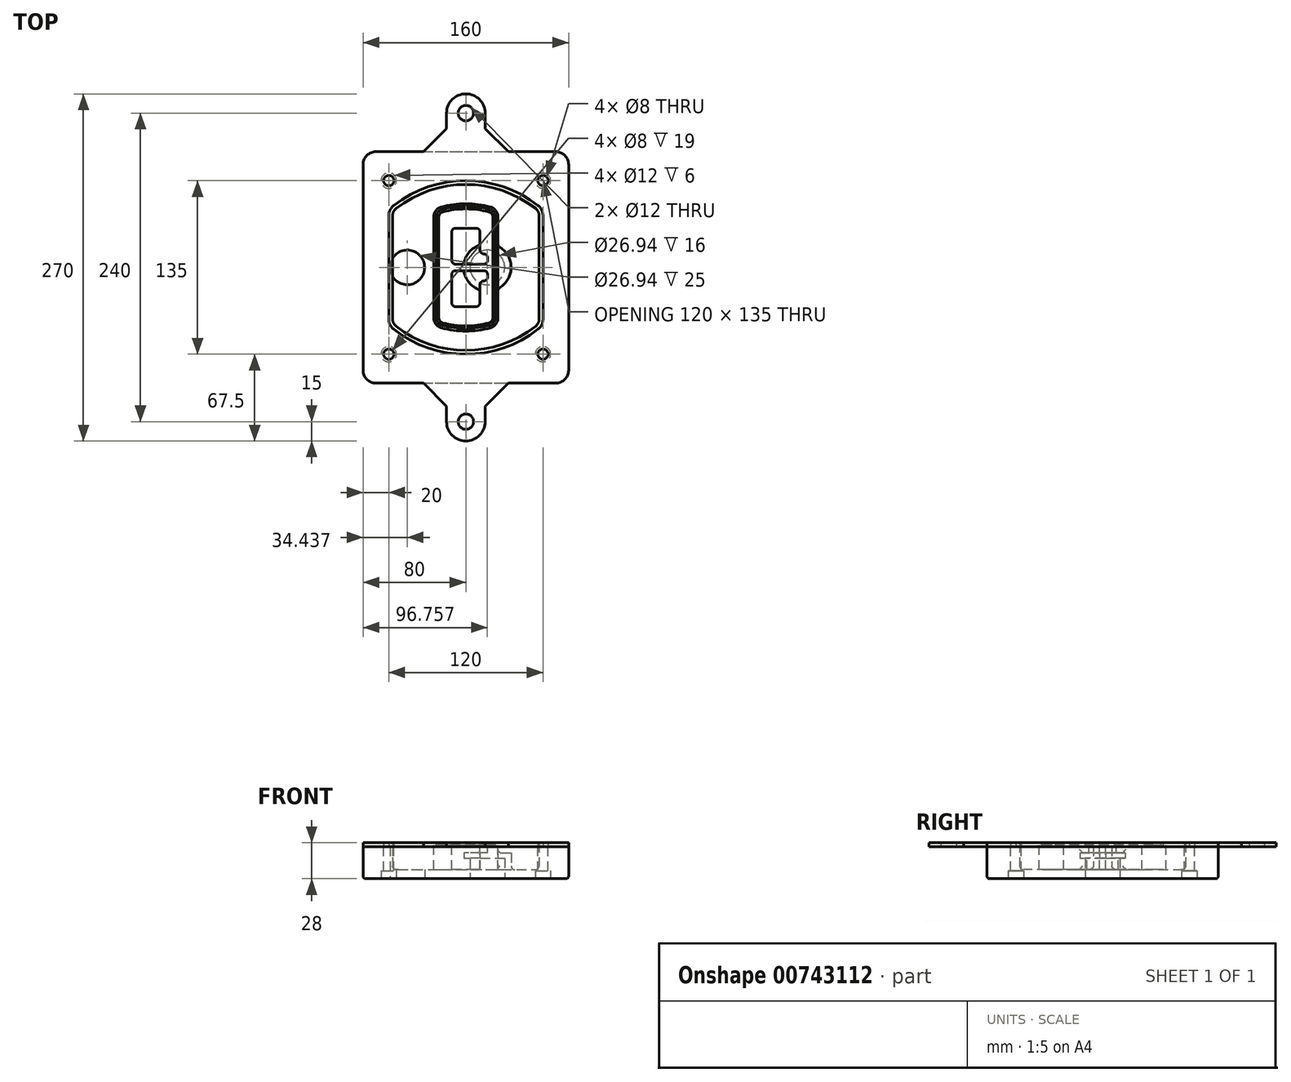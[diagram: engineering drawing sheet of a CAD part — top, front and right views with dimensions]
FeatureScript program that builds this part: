
annotation { "Feature Type Name" : "Feature", "Feature Type Description" : "" }
export const myFeature = defineFeature(function(context is Context, id is Id, definition is map)
    precondition{}
    {
        {
            var Q0;
            Q0=qCreatedBy(makeId("Top.planeOp"),FACE);
            var sketch = newSketch(context, id + "F0", { "sketchPlane" : qUnion([Q0])});
            skPoint(sketch, "E0.rect.middle", {"position": v(0, 0) * mm});
            skLineSegment(sketch, "E1.bottom", {"start": v(-70, -90) * mm, "end": v(70, -90) * mm});
            skLineSegment(sketch, "E1.top", {"start": v(-70, 90) * mm, "end": v(70, 90) * mm});
            skLineSegment(sketch, "E1.left", {"start": v(-80, -80) * mm, "end": v(-80, 80) * mm});
            skLineSegment(sketch, "E1.right", {"start": v(80, -80) * mm, "end": v(80, 80) * mm});
            skLineSegment(sketch, "E2", {"start": v(-80, 90) * mm, "end": v(80, -90) * mm, "construction": true});
            skLineSegment(sketch, "E3", {"start": v(80, 90) * mm, "end": v(-80, -90) * mm, "construction": true});
            skCircle(sketch, "E4", {"center": v(-60, 67.5) * mm, "radius": 4 * mm});
            skCircle(sketch, "E5", {"center": v(60, 67.5) * mm, "radius": 4 * mm});
            skCircle(sketch, "E6", {"center": v(60, -67.5) * mm, "radius": 4 * mm});
            skCircle(sketch, "E7", {"center": v(-60, -67.5) * mm, "radius": 4 * mm});
            skLineSegment(sketch, "E8", {"start": v(-60, 67.5) * mm, "end": v(60, 67.5) * mm, "construction": true});
            skLineSegment(sketch, "E9", {"start": v(60, 67.5) * mm, "end": v(60, -67.5) * mm, "construction": true});
            skLineSegment(sketch, "E10", {"start": v(60, -67.5) * mm, "end": v(-60, -67.5) * mm, "construction": true});
            skLineSegment(sketch, "E11", {"start": v(-60, -67.5) * mm, "end": v(-60, 67.5) * mm, "construction": true});
            skLineSegment(sketch, "E12", {"start": v(-60, 40.3) * mm, "end": v(-60, -40.3) * mm});
            skLineSegment(sketch, "E13", {"start": v(60, 40.3) * mm, "end": v(60, -40.3) * mm});
            skArc(sketch, "E14", {"start": v(56.15, 48.18) * mm, "mid": v(0, 67.5) * mm, "end": v(-56.15, 48.18) * mm});
            skArc(sketch, "E15", {"start": v(-56.15, -48.18) * mm, "mid": v(0, -67.5) * mm, "end": v(56.15, -48.18) * mm});
            skLineSegment(sketch, "E16", {"start": v(-60, 0) * mm, "end": v(60, 0) * mm, "construction": true});
            skPoint(sketch, "E17.visualSharp", {"position": v(-60, -45) * mm});
            skArc(sketch, "E17.filletArc", {"start": v(-60, -40.3) * mm, "mid": v(-58.99, -44.68) * mm, "end": v(-56.15, -48.18) * mm});
            skPoint(sketch, "E18.visualSharp", {"position": v(-60, 45) * mm});
            skArc(sketch, "E18.filletArc", {"start": v(-56.15, 48.18) * mm, "mid": v(-58.99, 44.68) * mm, "end": v(-60, 40.3) * mm});
            skPoint(sketch, "E19.visualSharp", {"position": v(60, 45) * mm});
            skArc(sketch, "E19.filletArc", {"start": v(60, 40.3) * mm, "mid": v(58.99, 44.68) * mm, "end": v(56.15, 48.18) * mm});
            skPoint(sketch, "E20.visualSharp", {"position": v(60, -45) * mm});
            skArc(sketch, "E20.filletArc", {"start": v(56.15, -48.18) * mm, "mid": v(58.99, -44.68) * mm, "end": v(60, -40.3) * mm});
            skPoint(sketch, "E21.visualSharp", {"position": v(-80, 90) * mm});
            skArc(sketch, "E21.filletArc", {"start": v(-70, 90) * mm, "mid": v(-77.07, 87.07) * mm, "end": v(-80, 80) * mm});
            skPoint(sketch, "E22.visualSharp", {"position": v(80, 90) * mm});
            skArc(sketch, "E22.filletArc", {"start": v(80, 80) * mm, "mid": v(77.07, 87.07) * mm, "end": v(70, 90) * mm});
            skPoint(sketch, "E23.visualSharp", {"position": v(80, -90) * mm});
            skArc(sketch, "E23.filletArc", {"start": v(70, -90) * mm, "mid": v(77.07, -87.07) * mm, "end": v(80, -80) * mm});
            skPoint(sketch, "E24.visualSharp", {"position": v(-80, -90) * mm});
            skArc(sketch, "E24.filletArc", {"start": v(-80, -80) * mm, "mid": v(-77.07, -87.07) * mm, "end": v(-70, -90) * mm});
            skArc(sketch, "E25.0", {"start": v(57, 40.3) * mm, "mid": v(56.3, 43.36) * mm, "end": v(54.3, 45.81) * mm});
            skLineSegment(sketch, "E25.1", {"start": v(57, 40.3) * mm, "end": v(57, -40.3) * mm});
            skArc(sketch, "E25.2", {"start": v(54.3, -45.81) * mm, "mid": v(56.3, -43.36) * mm, "end": v(57, -40.3) * mm});
            skArc(sketch, "E25.3", {"start": v(-54.3, -45.81) * mm, "mid": v(0, -64.5) * mm, "end": v(54.3, -45.81) * mm});
            skArc(sketch, "E25.4", {"start": v(-57, -40.3) * mm, "mid": v(-56.3, -43.36) * mm, "end": v(-54.3, -45.81) * mm});
            skArc(sketch, "E25.5", {"start": v(54.3, 45.81) * mm, "mid": v(0, 64.5) * mm, "end": v(-54.3, 45.81) * mm});
            skLineSegment(sketch, "E25.6", {"start": v(-57, 40.3) * mm, "end": v(-57, -40.3) * mm});
            skArc(sketch, "E25.7", {"start": v(-54.3, 45.81) * mm, "mid": v(-56.3, 43.36) * mm, "end": v(-57, 40.3) * mm});
            skArc(sketch, "E26.0", {"start": v(-58.62, 51.33) * mm, "mid": v(-62.58, 46.43) * mm, "end": v(-64, 40.3) * mm});
            skArc(sketch, "E26.1", {"start": v(58.62, 51.33) * mm, "mid": v(0, 71.5) * mm, "end": v(-58.62, 51.33) * mm});
            skArc(sketch, "E26.2", {"start": v(64, 40.3) * mm, "mid": v(62.58, 46.43) * mm, "end": v(58.62, 51.33) * mm});
            skLineSegment(sketch, "E26.3", {"start": v(64, 40.3) * mm, "end": v(64, -40.3) * mm});
            skArc(sketch, "E26.4", {"start": v(58.62, -51.33) * mm, "mid": v(62.58, -46.43) * mm, "end": v(64, -40.3) * mm});
            skLineSegment(sketch, "E26.5", {"start": v(-64, 40.3) * mm, "end": v(-64, -40.3) * mm});
            skArc(sketch, "E26.6", {"start": v(-58.62, -51.33) * mm, "mid": v(0, -71.5) * mm, "end": v(58.62, -51.33) * mm});
            skArc(sketch, "E26.7", {"start": v(-64, -40.3) * mm, "mid": v(-62.58, -46.43) * mm, "end": v(-58.62, -51.33) * mm});
            skSolve(sketch);
        }
        {
            var Q0;
            Q0=makeQuery(id+"F0.imprint","IMPRINT",FACE,{"disambiguationData":[TD([[makeQuery(id+"F0.imprint","IMPRINT",EDGE,{"derivedFrom":sQuery(id+"F0.wireOp",EDGE,"E1.bottom")}),1.0]])]});
            var Q1;
            Q1=makeQuery(id+"F0.imprint","IMPRINT",FACE,{"disambiguationData":[TD([[makeQuery(id+"F0.imprint","IMPRINT",EDGE,{"derivedFrom":sQuery(id+"F0.wireOp",EDGE,"E12")}),1.0]])]});
            var Q2;
            Q2=makeQuery(id+"F0.imprint","IMPRINT",FACE,{"disambiguationData":[TD([[makeQuery(id+"F0.imprint","IMPRINT",EDGE,{"derivedFrom":sQuery(id+"F0.wireOp",EDGE,"E25.0")}),1.0]])]});
            var Q3;
            Q3=makeQuery(id+"F0.imprint","IMPRINT",FACE,{"disambiguationData":[TD([[makeQuery(id+"F0.imprint","IMPRINT",EDGE,{"derivedFrom":sQuery(id+"F0.wireOp",EDGE,"E12")}),-1.0]])]});
            extrude(context, id + "F1", {"entities" : qUnion([Q0, Q1, Q2, Q3]), "oppositeDirection" : true, "depth" : 25 * mm});
        }
        {
            var Q0;
            Q0=makeQuery(id+"F0.imprint","IMPRINT",FACE,{"disambiguationData":[TD([[makeQuery(id+"F0.imprint","IMPRINT",EDGE,{"derivedFrom":sQuery(id+"F0.wireOp",EDGE,"E12")}),1.0]])]});
            extrude(context, id + "F2", {"entities" : qUnion([Q0]), "operationType" : NewBodyOperationType.ADD, "depth" : 3 * mm});
        }
        {
            var Q0;
            Q0=makeQuery(id+"F0.imprint","IMPRINT",FACE,{"disambiguationData":[TD([[makeQuery(id+"F0.imprint","IMPRINT",EDGE,{"derivedFrom":sQuery(id+"F0.wireOp",EDGE,"E25.0")}),1.0]])]});
            extrude(context, id + "F3", {"entities" : qUnion([Q0]), "operationType" : NewBodyOperationType.REMOVE, "oppositeDirection" : true, "depth" : 18 * mm});
        }
        {
            var Q0;
            Q0=makeQuery(id+"F2.opExtrude","CAP_FACE",FACE,{"disambiguationData":[OSD([sQuery(id+"F0.wireOp",EDGE,"E12"),sQuery(id+"F0.wireOp",EDGE,"E13"),sQuery(id+"F0.wireOp",EDGE,"E14"),sQuery(id+"F0.wireOp",EDGE,"E15"),sQuery(id+"F0.wireOp",EDGE,"E17.filletArc"),sQuery(id+"F0.wireOp",EDGE,"E18.filletArc"),sQuery(id+"F0.wireOp",EDGE,"E19.filletArc"),sQuery(id+"F0.wireOp",EDGE,"E20.filletArc"),sQuery(id+"F0.wireOp",EDGE,"E25.0"),sQuery(id+"F0.wireOp",EDGE,"E25.1"),sQuery(id+"F0.wireOp",EDGE,"E25.2"),sQuery(id+"F0.wireOp",EDGE,"E25.3"),sQuery(id+"F0.wireOp",EDGE,"E25.4"),sQuery(id+"F0.wireOp",EDGE,"E25.5"),sQuery(id+"F0.wireOp",EDGE,"E25.6"),sQuery(id+"F0.wireOp",EDGE,"E25.7")])],"isStart":false});
            var sketch = newSketch(context, id + "F4", { "sketchPlane" : qUnion([Q0])});
            skArc(sketch, "E27.0", {"start": v(-19.08, -46.97) * mm, "mid": v(0, -49.5) * mm, "end": v(19.08, -46.97) * mm});
            skArc(sketch, "E28.0", {"start": v(19.08, 46.97) * mm, "mid": v(0, 49.5) * mm, "end": v(-19.08, 46.97) * mm});
            skLineSegment(sketch, "E29", {"start": v(-25, 39.25) * mm, "end": v(-25, -39.25) * mm});
            skLineSegment(sketch, "E30", {"start": v(25, 39.25) * mm, "end": v(25, -39.25) * mm});
            skLineSegment(sketch, "E31", {"start": v(-25, 45.1) * mm, "end": v(25, 45.1) * mm, "construction": true});
            skLineSegment(sketch, "E32", {"start": v(-25, -45.1) * mm, "end": v(25, -45.1) * mm, "construction": true});
            skPoint(sketch, "E33.visualSharp", {"position": v(-25, 45.1) * mm});
            skArc(sketch, "E33.filletArc", {"start": v(-19.08, 46.97) * mm, "mid": v(-23.35, 44.11) * mm, "end": v(-25, 39.25) * mm});
            skPoint(sketch, "E34.visualSharp", {"position": v(25, 45.1) * mm});
            skArc(sketch, "E34.filletArc", {"start": v(25, 39.25) * mm, "mid": v(23.35, 44.11) * mm, "end": v(19.08, 46.97) * mm});
            skPoint(sketch, "E35.visualSharp", {"position": v(25, -45.1) * mm});
            skArc(sketch, "E35.filletArc", {"start": v(19.08, -46.97) * mm, "mid": v(23.35, -44.11) * mm, "end": v(25, -39.25) * mm});
            skPoint(sketch, "E36.visualSharp", {"position": v(-25, -45.1) * mm});
            skArc(sketch, "E36.filletArc", {"start": v(-25, -39.25) * mm, "mid": v(-23.35, -44.11) * mm, "end": v(-19.08, -46.97) * mm});
            skArc(sketch, "E37.0", {"start": v(54.3, 45.81) * mm, "mid": v(0, 64.5) * mm, "end": v(-54.3, 45.81) * mm});
            skArc(sketch, "E37.1", {"start": v(-54.3, 45.81) * mm, "mid": v(-56.3, 43.36) * mm, "end": v(-57, 40.3) * mm});
            skLineSegment(sketch, "E37.2", {"start": v(-57, 40.3) * mm, "end": v(-57, -40.3) * mm});
            skArc(sketch, "E37.3", {"start": v(-57, -40.3) * mm, "mid": v(-56.3, -43.36) * mm, "end": v(-54.3, -45.81) * mm});
            skArc(sketch, "E37.4", {"start": v(-54.3, -45.81) * mm, "mid": v(0, -64.5) * mm, "end": v(54.3, -45.81) * mm});
            skArc(sketch, "E37.5", {"start": v(54.3, -45.81) * mm, "mid": v(56.3, -43.36) * mm, "end": v(57, -40.3) * mm});
            skLineSegment(sketch, "E37.6", {"start": v(57, 40.3) * mm, "end": v(57, -40.3) * mm});
            skArc(sketch, "E37.7", {"start": v(57, 40.3) * mm, "mid": v(56.3, 43.36) * mm, "end": v(54.3, 45.81) * mm});
            skLineSegment(sketch, "E38.0", {"start": v(23, 39.25) * mm, "end": v(23, -39.25) * mm});
            skArc(sketch, "E38.1", {"start": v(18.56, -45.04) * mm, "mid": v(21.76, -42.9) * mm, "end": v(23, -39.25) * mm});
            skArc(sketch, "E38.2", {"start": v(-18.56, -45.04) * mm, "mid": v(0, -47.5) * mm, "end": v(18.56, -45.04) * mm});
            skArc(sketch, "E38.3", {"start": v(-23, -39.25) * mm, "mid": v(-21.76, -42.9) * mm, "end": v(-18.56, -45.04) * mm});
            skLineSegment(sketch, "E38.4", {"start": v(-23, 39.25) * mm, "end": v(-23, -39.25) * mm});
            skArc(sketch, "E38.5", {"start": v(23, 39.25) * mm, "mid": v(21.76, 42.9) * mm, "end": v(18.56, 45.04) * mm});
            skArc(sketch, "E38.6", {"start": v(-18.56, 45.04) * mm, "mid": v(-21.76, 42.9) * mm, "end": v(-23, 39.25) * mm});
            skArc(sketch, "E38.7", {"start": v(18.56, 45.04) * mm, "mid": v(0, 47.5) * mm, "end": v(-18.56, 45.04) * mm});
            skArc(sketch, "E39.0", {"start": v(21, 39.25) * mm, "mid": v(20.18, 41.68) * mm, "end": v(18.04, 43.1) * mm});
            skLineSegment(sketch, "E39.1", {"start": v(21, 39.25) * mm, "end": v(21, -39.25) * mm});
            skArc(sketch, "E39.2", {"start": v(18.04, -43.1) * mm, "mid": v(20.18, -41.68) * mm, "end": v(21, -39.25) * mm});
            skArc(sketch, "E39.3", {"start": v(-18.04, -43.1) * mm, "mid": v(0, -45.5) * mm, "end": v(18.04, -43.1) * mm});
            skArc(sketch, "E39.4", {"start": v(-21, -39.25) * mm, "mid": v(-20.18, -41.68) * mm, "end": v(-18.04, -43.1) * mm});
            skArc(sketch, "E39.5", {"start": v(18.04, 43.1) * mm, "mid": v(0, 45.5) * mm, "end": v(-18.04, 43.1) * mm});
            skLineSegment(sketch, "E39.6", {"start": v(-21, 39.25) * mm, "end": v(-21, -39.25) * mm});
            skArc(sketch, "E39.7", {"start": v(-18.04, 43.1) * mm, "mid": v(-20.18, 41.68) * mm, "end": v(-21, 39.25) * mm});
            skLineSegment(sketch, "E40", {"start": v(-25, 0) * mm, "end": v(25, 0) * mm, "construction": true});
            skLineSegment(sketch, "E41", {"start": v(-11, 5.5) * mm, "end": v(-11, 27.5) * mm});
            skLineSegment(sketch, "E42", {"start": v(-8, 30.5) * mm, "end": v(8, 30.5) * mm});
            skLineSegment(sketch, "E43", {"start": v(11, 27.5) * mm, "end": v(11, 13.5) * mm});
            skLineSegment(sketch, "E44", {"start": v(14, 10.5) * mm, "end": v(14, 10.5) * mm});
            skLineSegment(sketch, "E45", {"start": v(17, 7.5) * mm, "end": v(17, 5.5) * mm});
            skLineSegment(sketch, "E46", {"start": v(14, 2.5) * mm, "end": v(-8, 2.5) * mm});
            skPoint(sketch, "E47.visualSharp", {"position": v(-11, 30.5) * mm});
            skArc(sketch, "E47.filletArc", {"start": v(-8, 30.5) * mm, "mid": v(-10.12, 29.62) * mm, "end": v(-11, 27.5) * mm});
            skPoint(sketch, "E48.visualSharp", {"position": v(11, 30.5) * mm});
            skArc(sketch, "E48.filletArc", {"start": v(11, 27.5) * mm, "mid": v(10.12, 29.62) * mm, "end": v(8, 30.5) * mm});
            skPoint(sketch, "E49.visualSharp", {"position": v(11, 10.5) * mm});
            skArc(sketch, "E49.filletArc", {"start": v(11, 13.5) * mm, "mid": v(11.88, 11.38) * mm, "end": v(14, 10.5) * mm});
            skPoint(sketch, "E50.visualSharp", {"position": v(17, 10.5) * mm});
            skArc(sketch, "E50.filletArc", {"start": v(17, 7.5) * mm, "mid": v(16.12, 9.62) * mm, "end": v(14, 10.5) * mm});
            skPoint(sketch, "E51.visualSharp", {"position": v(17, 2.5) * mm});
            skArc(sketch, "E51.filletArc", {"start": v(14, 2.5) * mm, "mid": v(16.12, 3.38) * mm, "end": v(17, 5.5) * mm});
            skPoint(sketch, "E52.visualSharp", {"position": v(-11, 2.5) * mm});
            skArc(sketch, "E52.filletArc", {"start": v(-11, 5.5) * mm, "mid": v(-10.12, 3.38) * mm, "end": v(-8, 2.5) * mm});
            skLineSegment(sketch, "E53.0.MirrorCS", {"start": v(14, -2.5) * mm, "end": v(-8, -2.5) * mm});
            skArc(sketch, "E54.0.MirrorCS", {"start": v(-11, -5.5) * mm, "mid": v(-10.12, -3.38) * mm, "end": v(-8, -2.5) * mm});
            skLineSegment(sketch, "E55.0.MirrorCS", {"start": v(-11, -5.5) * mm, "end": v(-11, -27.5) * mm});
            skArc(sketch, "E56.0.MirrorCS", {"start": v(-8, -30.5) * mm, "mid": v(-10.12, -29.62) * mm, "end": v(-11, -27.5) * mm});
            skLineSegment(sketch, "E57.0.MirrorCS", {"start": v(-8, -30.5) * mm, "end": v(8, -30.5) * mm});
            skArc(sketch, "E58.0.MirrorCS", {"start": v(11, -27.5) * mm, "mid": v(10.12, -29.62) * mm, "end": v(8, -30.5) * mm});
            skLineSegment(sketch, "E59.0.MirrorCS", {"start": v(11, -27.5) * mm, "end": v(11, -13.5) * mm});
            skArc(sketch, "E60.0.MirrorCS", {"start": v(11, -13.5) * mm, "mid": v(11.88, -11.38) * mm, "end": v(14, -10.5) * mm});
            skArc(sketch, "E61.0.MirrorCS", {"start": v(17, -7.5) * mm, "mid": v(16.12, -9.62) * mm, "end": v(14, -10.5) * mm});
            skLineSegment(sketch, "E62.0.MirrorCS", {"start": v(17, -7.5) * mm, "end": v(17, -5.5) * mm});
            skArc(sketch, "E63.0.MirrorCS", {"start": v(14, -2.5) * mm, "mid": v(16.12, -3.38) * mm, "end": v(17, -5.5) * mm});
            skSolve(sketch);
        }
        {
            var Q0;
            Q0=makeQuery(id+"F4.imprint","IMPRINT",FACE,{"disambiguationData":[TD([[makeQuery(id+"F4.imprint","IMPRINT",EDGE,{"derivedFrom":sQuery(id+"F4.wireOp",EDGE,"E27.0")}),1.0]])]});
            var Q1;
            Q1=makeQuery(id+"F4.imprint","IMPRINT",FACE,{"disambiguationData":[TD([[makeQuery(id+"F4.imprint","IMPRINT",EDGE,{"derivedFrom":sQuery(id+"F4.wireOp",EDGE,"E38.0")}),-1.0]])]});
            var Q2;
            Q2=makeQuery(id+"F4.imprint","IMPRINT",FACE,{"disambiguationData":[TD([[makeQuery(id+"F4.imprint","IMPRINT",EDGE,{"derivedFrom":sQuery(id+"F4.wireOp",EDGE,"E39.0")}),1.0]])]});
            extrude(context, id + "F5", {"entities" : qUnion([Q0, Q1, Q2]), "operationType" : NewBodyOperationType.ADD, "endBound" : BoundingType.UP_TO_NEXT, "oppositeDirection" : true, "depth" : 25 * mm});
        }
        {
            var Q0;
            Q0=makeQuery(id+"F4.imprint","IMPRINT",FACE,{"disambiguationData":[TD([[makeQuery(id+"F4.imprint","IMPRINT",EDGE,{"derivedFrom":sQuery(id+"F4.wireOp",EDGE,"E38.0")}),-1.0]])]});
            extrude(context, id + "F6", {"entities" : qUnion([Q0]), "operationType" : NewBodyOperationType.REMOVE, "oppositeDirection" : true, "depth" : 2 * mm});
        }
        {
            var Q0;
            Q0=makeQuery(id+"F1.opExtrude","CAP_FACE",FACE,{"disambiguationData":[OSD([sQuery(id+"F0.wireOp",EDGE,"E1.bottom"),sQuery(id+"F0.wireOp",EDGE,"E1.top"),sQuery(id+"F0.wireOp",EDGE,"E1.left"),sQuery(id+"F0.wireOp",EDGE,"E1.right"),sQuery(id+"F0.wireOp",EDGE,"E4"),sQuery(id+"F0.wireOp",EDGE,"E5"),sQuery(id+"F0.wireOp",EDGE,"E6"),sQuery(id+"F0.wireOp",EDGE,"E7"),sQuery(id+"F0.wireOp",EDGE,"E21.filletArc"),sQuery(id+"F0.wireOp",EDGE,"E22.filletArc"),sQuery(id+"F0.wireOp",EDGE,"E23.filletArc"),sQuery(id+"F0.wireOp",EDGE,"E24.filletArc")])],"isStart":false});
            var sketch = newSketch(context, id + "F7", { "sketchPlane" : qUnion([Q0])});
            skCircle(sketch, "E64", {"center": v(16.76, 0) * mm, "radius": 13.47 * mm});
            skCircle(sketch, "E65", {"center": v(-45.56, 0) * mm, "radius": 13.47 * mm});
            skLineSegment(sketch, "E66", {"start": v(80, 0) * mm, "end": v(-80, 0) * mm});
            skCircle(sketch, "E67", {"center": v(16.76, 0) * mm, "radius": 18.47 * mm});
            skCircle(sketch, "E68", {"center": v(60, -67.5) * mm, "radius": 6 * mm});
            skCircle(sketch, "E69", {"center": v(-60, -67.5) * mm, "radius": 6 * mm});
            skCircle(sketch, "E70", {"center": v(-60, 67.5) * mm, "radius": 6 * mm});
            skCircle(sketch, "E71", {"center": v(60, 67.5) * mm, "radius": 6 * mm});
            skSolve(sketch);
        }
        {
            var Q0;
            {var subQ1=sQuery(id+"F7.wireOp",EDGE,"E66");var subQ4=sQuery(id+"F7.wireOp",EDGE,"E64");var subQ6=makeQuery(id+"F7.imprint","INTERSECT",VERTEX,{"disambiguationData":[OD(0.0)],"derivedFrom":[subQ4,subQ1]});Q0=makeQuery(id+"F7.imprint","IMPRINT",FACE,{"disambiguationData":[TD([[makeQuery(id+"F7.imprint","IMPRINT",EDGE,{"disambiguationData":[TD([[subQ6,-1.0]])],"derivedFrom":subQ4}),-1.0]])]});}
            var Q1;
            {var subQ0=sQuery(id+"F7.wireOp",EDGE,"E66");var subQ1=sQuery(id+"F7.wireOp",EDGE,"E64");var subQ3=makeQuery(id+"F7.imprint","INTERSECT",VERTEX,{"disambiguationData":[OD(0.0)],"derivedFrom":[subQ1,subQ0]});Q1=makeQuery(id+"F7.imprint","IMPRINT",FACE,{"disambiguationData":[TD([[makeQuery(id+"F7.imprint","IMPRINT",EDGE,{"disambiguationData":[TD([[subQ3,-1.0]])],"derivedFrom":subQ1}),1.0]])]});}
            var Q2;
            {var subQ0=sQuery(id+"F7.wireOp",EDGE,"E66");var subQ1=sQuery(id+"F7.wireOp",EDGE,"E64");var subQ3=makeQuery(id+"F7.imprint","INTERSECT",VERTEX,{"disambiguationData":[OD(0.0)],"derivedFrom":[subQ1,subQ0]});Q2=makeQuery(id+"F7.imprint","IMPRINT",FACE,{"disambiguationData":[TD([[makeQuery(id+"F7.imprint","IMPRINT",EDGE,{"disambiguationData":[TD([[subQ3,1.0]])],"derivedFrom":subQ1}),1.0]])]});}
            var Q3;
            {var subQ1=sQuery(id+"F7.wireOp",EDGE,"E66");var subQ4=sQuery(id+"F7.wireOp",EDGE,"E64");var subQ6=makeQuery(id+"F7.imprint","INTERSECT",VERTEX,{"disambiguationData":[OD(0.0)],"derivedFrom":[subQ4,subQ1]});Q3=makeQuery(id+"F7.imprint","IMPRINT",FACE,{"disambiguationData":[TD([[makeQuery(id+"F7.imprint","IMPRINT",EDGE,{"disambiguationData":[TD([[subQ6,1.0]])],"derivedFrom":subQ4}),-1.0]])]});}
            extrude(context, id + "F8", {"entities" : qUnion([Q0, Q1, Q2, Q3]), "operationType" : NewBodyOperationType.ADD, "oppositeDirection" : true, "depth" : 20 * mm});
        }
        {
            var Q0;
            {var subQ0=sQuery(id+"F7.wireOp",EDGE,"E66");var subQ1=sQuery(id+"F7.wireOp",EDGE,"E64");var subQ3=makeQuery(id+"F7.imprint","INTERSECT",VERTEX,{"disambiguationData":[OD(0.0)],"derivedFrom":[subQ1,subQ0]});Q0=makeQuery(id+"F7.imprint","IMPRINT",FACE,{"disambiguationData":[TD([[makeQuery(id+"F7.imprint","IMPRINT",EDGE,{"disambiguationData":[TD([[subQ3,-1.0]])],"derivedFrom":subQ1}),1.0]])]});}
            var Q1;
            {var subQ0=sQuery(id+"F7.wireOp",EDGE,"E66");var subQ1=sQuery(id+"F7.wireOp",EDGE,"E64");var subQ3=makeQuery(id+"F7.imprint","INTERSECT",VERTEX,{"disambiguationData":[OD(0.0)],"derivedFrom":[subQ1,subQ0]});Q1=makeQuery(id+"F7.imprint","IMPRINT",FACE,{"disambiguationData":[TD([[makeQuery(id+"F7.imprint","IMPRINT",EDGE,{"disambiguationData":[TD([[subQ3,1.0]])],"derivedFrom":subQ1}),1.0]])]});}
            extrude(context, id + "F9", {"entities" : qUnion([Q0, Q1]), "operationType" : NewBodyOperationType.REMOVE, "oppositeDirection" : true, "depth" : 16 * mm});
        }
        {
            var Q0;
            {var subQ0=sQuery(id+"F7.wireOp",EDGE,"E66");var subQ1=sQuery(id+"F7.wireOp",EDGE,"E65");var subQ3=makeQuery(id+"F7.imprint","INTERSECT",VERTEX,{"disambiguationData":[OD(0.0)],"derivedFrom":[subQ1,subQ0]});Q0=makeQuery(id+"F7.imprint","IMPRINT",FACE,{"disambiguationData":[TD([[makeQuery(id+"F7.imprint","IMPRINT",EDGE,{"disambiguationData":[TD([[subQ3,-1.0]])],"derivedFrom":subQ1}),1.0]])]});}
            var Q1;
            {var subQ0=sQuery(id+"F7.wireOp",EDGE,"E66");var subQ1=sQuery(id+"F7.wireOp",EDGE,"E65");var subQ3=makeQuery(id+"F7.imprint","INTERSECT",VERTEX,{"disambiguationData":[OD(0.0)],"derivedFrom":[subQ1,subQ0]});Q1=makeQuery(id+"F7.imprint","IMPRINT",FACE,{"disambiguationData":[TD([[makeQuery(id+"F7.imprint","IMPRINT",EDGE,{"disambiguationData":[TD([[subQ3,1.0]])],"derivedFrom":subQ1}),1.0]])]});}
            extrude(context, id + "F10", {"entities" : qUnion([Q0, Q1]), "operationType" : NewBodyOperationType.REMOVE, "oppositeDirection" : true, "depth" : 25 * mm, "offsetDistance" : 25 * mm});
        }
        {
            var Q0;
            Q0=makeQuery(id+"F7.imprint","IMPRINT",FACE,{"disambiguationData":[TD([[makeQuery(id+"F7.imprint","IMPRINT",EDGE,{"derivedFrom":sQuery(id+"F7.wireOp",EDGE,"E68")}),1.0]])]});
            var Q1;
            Q1=makeQuery(id+"F7.imprint","IMPRINT",FACE,{"disambiguationData":[TD([[makeQuery(id+"F7.imprint","IMPRINT",EDGE,{"derivedFrom":makeQuery(id+"F1.opExtrude","CAP_EDGE",EDGE,{"disambiguationData":[OSD([sQuery(id+"F0.wireOp",EDGE,"E5")])],"isStart":false})}),-1.0]])]});
            var Q2;
            Q2=makeQuery(id+"F7.imprint","IMPRINT",FACE,{"disambiguationData":[TD([[makeQuery(id+"F7.imprint","IMPRINT",EDGE,{"derivedFrom":sQuery(id+"F7.wireOp",EDGE,"E69")}),1.0]])]});
            var Q3;
            Q3=makeQuery(id+"F7.imprint","IMPRINT",FACE,{"disambiguationData":[TD([[makeQuery(id+"F7.imprint","IMPRINT",EDGE,{"derivedFrom":makeQuery(id+"F1.opExtrude","CAP_EDGE",EDGE,{"disambiguationData":[OSD([sQuery(id+"F0.wireOp",EDGE,"E4")])],"isStart":false})}),-1.0]])]});
            var Q4;
            Q4=makeQuery(id+"F7.imprint","IMPRINT",FACE,{"disambiguationData":[TD([[makeQuery(id+"F7.imprint","IMPRINT",EDGE,{"derivedFrom":sQuery(id+"F7.wireOp",EDGE,"E70")}),1.0]])]});
            var Q5;
            Q5=makeQuery(id+"F7.imprint","IMPRINT",FACE,{"disambiguationData":[TD([[makeQuery(id+"F7.imprint","IMPRINT",EDGE,{"derivedFrom":makeQuery(id+"F1.opExtrude","CAP_EDGE",EDGE,{"disambiguationData":[OSD([sQuery(id+"F0.wireOp",EDGE,"E7")])],"isStart":false})}),-1.0]])]});
            var Q6;
            Q6=makeQuery(id+"F7.imprint","IMPRINT",FACE,{"disambiguationData":[TD([[makeQuery(id+"F7.imprint","IMPRINT",EDGE,{"derivedFrom":sQuery(id+"F7.wireOp",EDGE,"E71")}),1.0]])]});
            var Q7;
            Q7=makeQuery(id+"F7.imprint","IMPRINT",FACE,{"disambiguationData":[TD([[makeQuery(id+"F7.imprint","IMPRINT",EDGE,{"derivedFrom":makeQuery(id+"F1.opExtrude","CAP_EDGE",EDGE,{"disambiguationData":[OSD([sQuery(id+"F0.wireOp",EDGE,"E6")])],"isStart":false})}),-1.0]])]});
            extrude(context, id + "F11", {"entities" : qUnion([Q0, Q1, Q2, Q3, Q4, Q5, Q6, Q7]), "operationType" : NewBodyOperationType.REMOVE, "oppositeDirection" : true, "depth" : 6 * mm});
        }
        {
            var Q0;
            Q0=makeQuery(id+"F9.boolean.opBoolean","COPY",FACE,{"derivedFrom":makeQuery(id+"F9.opExtrude","CAP_FACE",FACE,{"disambiguationData":[OSD([sQuery(id+"F7.wireOp",EDGE,"E64")])],"isStart":false})});
            var sketch = newSketch(context, id + "F12", { "sketchPlane" : qUnion([Q0])});
            skArc(sketch, "E72.0", {"start": v(11, 17.55) * mm, "mid": v(2.57, 11.82) * mm, "end": v(-1.54, 2.5) * mm});
            skArc(sketch, "E72.1", {"start": v(-1.54, -2.5) * mm, "mid": v(2.57, -11.82) * mm, "end": v(11, -17.55) * mm});
            skLineSegment(sketch, "E73", {"start": v(-1.54, -2.5) * mm, "end": v(14, -2.5) * mm});
            skLineSegment(sketch, "E74.0", {"start": v(14, 2.5) * mm, "end": v(-1.54, 2.5) * mm});
            skArc(sketch, "E74.1", {"start": v(14, 2.5) * mm, "mid": v(16.12, 3.38) * mm, "end": v(17, 5.5) * mm});
            skLineSegment(sketch, "E74.2", {"start": v(17, 7.5) * mm, "end": v(17, 5.5) * mm});
            skArc(sketch, "E74.3", {"start": v(17, 7.5) * mm, "mid": v(16.12, 9.62) * mm, "end": v(14, 10.5) * mm});
            skArc(sketch, "E74.4", {"start": v(11, 13.5) * mm, "mid": v(11.88, 11.38) * mm, "end": v(14, 10.5) * mm});
            skLineSegment(sketch, "E74.5", {"start": v(11, 17.55) * mm, "end": v(11, 13.5) * mm});
            skLineSegment(sketch, "E74.7", {"start": v(14, -2.5) * mm, "end": v(-1.54, -2.5) * mm});
            skArc(sketch, "E74.8", {"start": v(14, -2.5) * mm, "mid": v(16.12, -3.38) * mm, "end": v(17, -5.5) * mm});
            skLineSegment(sketch, "E74.9", {"start": v(17, -7.5) * mm, "end": v(17, -5.5) * mm});
            skArc(sketch, "E74.10", {"start": v(17, -7.5) * mm, "mid": v(16.12, -9.62) * mm, "end": v(14, -10.5) * mm});
            skArc(sketch, "E74.11", {"start": v(11, -13.5) * mm, "mid": v(11.88, -11.38) * mm, "end": v(14, -10.5) * mm});
            skLineSegment(sketch, "E74.12", {"start": v(11, -17.55) * mm, "end": v(11, -13.5) * mm});
            skPoint(sketch, "E75.orphan", {"position": v(11, -27.5) * mm});
            skPoint(sketch, "E76.orphan", {"position": v(-8, -2.5) * mm});
            skPoint(sketch, "E77.orphan", {"position": v(-8, 2.5) * mm});
            skPoint(sketch, "E78.orphan", {"position": v(11, 27.5) * mm});
            skSolve(sketch);
        }
        {
            var Q0;
            {var subQ7=sQuery(id+"F12.wireOp",EDGE,"E72.0");var subQ14=sQuery(id+"F12.wireOp",EDGE,"E72.1");var subQ16=sQuery(id+"F12.wireOp",EDGE,"E74.1");var subQ18=sQuery(id+"F12.wireOp",EDGE,"E74.8");Q0=qUnion([makeQuery(id+"F12.imprint","IMPRINT",FACE,{"disambiguationData":[TD([[makeQuery(id+"F12.imprint","IMPRINT",EDGE,{"derivedFrom":subQ7}),1.0]])]}),makeQuery(id+"F12.imprint","IMPRINT",FACE,{"disambiguationData":[TD([[makeQuery(id+"F12.imprint","IMPRINT",EDGE,{"derivedFrom":subQ14}),1.0]])]}),makeQuery(id+"F12.imprint","IMPRINT",FACE,{"disambiguationData":[TD([[makeQuery(id+"F12.imprint","IMPRINT",EDGE,{"derivedFrom":subQ16}),1.0]])]}),makeQuery(id+"F12.imprint","IMPRINT",FACE,{"disambiguationData":[TD([[makeQuery(id+"F12.imprint","IMPRINT",EDGE,{"derivedFrom":subQ18}),-1.0]])]})]);}
            var Q1;
            Q1=makeQuery(id+"F5.boolean.opBoolean","SPLIT",FACE,{"disambiguationData":[TD([makeQuery(id+"F5.opExtrude","SWEPT_FACE",FACE,{"disambiguationData":[OSD([sQuery(id+"F4.wireOp",EDGE,"E41")])]})])],"derivedFrom":makeQuery(id+"F3.boolean.opBoolean","COPY",FACE,{"derivedFrom":makeQuery(id+"F3.opExtrude","CAP_FACE",FACE,{"disambiguationData":[OSD([sQuery(id+"F0.wireOp",EDGE,"E25.0"),sQuery(id+"F0.wireOp",EDGE,"E25.1"),sQuery(id+"F0.wireOp",EDGE,"E25.2"),sQuery(id+"F0.wireOp",EDGE,"E25.3"),sQuery(id+"F0.wireOp",EDGE,"E25.4"),sQuery(id+"F0.wireOp",EDGE,"E25.5"),sQuery(id+"F0.wireOp",EDGE,"E25.6"),sQuery(id+"F0.wireOp",EDGE,"E25.7")])],"isStart":false})})});
            extrude(context, id + "F13", {"entities" : qUnion([Q0]), "operationType" : NewBodyOperationType.REMOVE, "endBound" : BoundingType.UP_TO_SURFACE, "endBoundEntityFace" : qUnion([Q1]), "depth" : 25 * mm});
        }
        {
            var Q0;
            Q0=makeQuery(id+"F3.boolean.opBoolean","COPY",EDGE,{"derivedFrom":makeQuery(id+"F3.opExtrude","CAP_EDGE",EDGE,{"disambiguationData":[OSD([sQuery(id+"F0.wireOp",EDGE,"E25.6")])],"isStart":false})});
            var Q1;
            Q1=makeQuery(id+"F8.boolean.opBoolean","INTERSECT",EDGE,{"derivedFrom":[makeQuery(id+"F5.opExtrude","SWEPT_FACE",FACE,{"disambiguationData":[OSD([sQuery(id+"F4.wireOp",EDGE,"E30")])]}),makeQuery(id+"F8.opExtrude","CAP_FACE",FACE,{"disambiguationData":[OSD([sQuery(id+"F7.wireOp",EDGE,"E67")])],"isStart":false})]});
            var Q2;
            Q2=makeQuery(id+"F8.boolean.opBoolean","INTERSECT",EDGE,{"disambiguationData":[OD(1.0)],"derivedFrom":[makeQuery(id+"F5.opExtrude","SWEPT_FACE",FACE,{"disambiguationData":[OSD([sQuery(id+"F4.wireOp",EDGE,"E30")])]}),makeQuery(id+"F8.opExtrude","SWEPT_FACE",FACE,{"disambiguationData":[OSD([sQuery(id+"F7.wireOp",EDGE,"E67")])]})]});
            var Q3;
            {var subQ0=makeQuery(id+"F3.boolean.opBoolean","COPY",FACE,{"derivedFrom":makeQuery(id+"F3.opExtrude","CAP_FACE",FACE,{"disambiguationData":[OSD([sQuery(id+"F0.wireOp",EDGE,"E25.0"),sQuery(id+"F0.wireOp",EDGE,"E25.1"),sQuery(id+"F0.wireOp",EDGE,"E25.2"),sQuery(id+"F0.wireOp",EDGE,"E25.3"),sQuery(id+"F0.wireOp",EDGE,"E25.4"),sQuery(id+"F0.wireOp",EDGE,"E25.5"),sQuery(id+"F0.wireOp",EDGE,"E25.6"),sQuery(id+"F0.wireOp",EDGE,"E25.7")])],"isStart":false})});var subQ1=sQuery(id+"F4.wireOp",EDGE,"E30");Q3=makeQuery(id+"F8.boolean.opBoolean","SPLIT",EDGE,{"disambiguationData":[TD([makeQuery(id+"F5.opExtrude","SWEPT_FACE",FACE,{"disambiguationData":[OSD([sQuery(id+"F4.wireOp",EDGE,"E35.filletArc")])]})])],"derivedFrom":makeQuery(id+"F5.opExtrude","TWEAK_EDGE",EDGE,{"derivedFrom":[subQ0,makeQuery(id+"F4.imprint","IMPRINT",EDGE,{"derivedFrom":subQ1})]})});}
            var Q4;
            {var subQ0=sQuery(id+"F0.wireOp",EDGE,"E25.0");var subQ1=sQuery(id+"F0.wireOp",EDGE,"E25.1");var subQ2=sQuery(id+"F0.wireOp",EDGE,"E25.2");var subQ3=sQuery(id+"F0.wireOp",EDGE,"E25.3");var subQ4=sQuery(id+"F0.wireOp",EDGE,"E25.4");var subQ5=sQuery(id+"F0.wireOp",EDGE,"E25.5");var subQ6=sQuery(id+"F0.wireOp",EDGE,"E25.6");var subQ7=sQuery(id+"F0.wireOp",EDGE,"E25.7");Q4=makeQuery(id+"F8.boolean.opBoolean","INTERSECT",EDGE,{"derivedFrom":[makeQuery(id+"F5.boolean.opBoolean","SPLIT",FACE,{"disambiguationData":[TD([makeQuery(id+"F2.opExtrude","SWEPT_FACE",FACE,{"disambiguationData":[OSD([subQ0])]})])],"derivedFrom":makeQuery(id+"F3.boolean.opBoolean","COPY",FACE,{"derivedFrom":makeQuery(id+"F3.opExtrude","CAP_FACE",FACE,{"disambiguationData":[OSD([subQ0,subQ1,subQ2,subQ3,subQ4,subQ5,subQ6,subQ7])],"isStart":false})})}),makeQuery(id+"F8.opExtrude","SWEPT_FACE",FACE,{"disambiguationData":[OSD([sQuery(id+"F7.wireOp",EDGE,"E67")])]})]});}
            var Q5;
            Q5=makeQuery(id+"F8.boolean.opBoolean","INTERSECT",EDGE,{"disambiguationData":[OD(0.0)],"derivedFrom":[makeQuery(id+"F5.opExtrude","SWEPT_FACE",FACE,{"disambiguationData":[OSD([sQuery(id+"F4.wireOp",EDGE,"E30")])]}),makeQuery(id+"F8.opExtrude","SWEPT_FACE",FACE,{"disambiguationData":[OSD([sQuery(id+"F7.wireOp",EDGE,"E67")])]})]});
            fillet(context, id + "F14", {"entities" : qUnion([Q0, Q1, Q2, Q3, Q4, Q5]), "radius" : 3 * mm, "tangentPropagation" : true, "allowEdgeOverflow" : false});
        }
        {
            var Q0;
            Q0=makeQuery(id+"F1.opExtrude","CAP_EDGE",EDGE,{"disambiguationData":[OSD([sQuery(id+"F0.wireOp",EDGE,"E1.bottom")])],"isStart":false});
            fillet(context, id + "F15", {"entities" : qUnion([Q0]), "radius" : 2 * mm, "tangentPropagation" : true, "allowEdgeOverflow" : false});
        }
        {
            var Q0;
            {var subQ0=sQuery(id+"F0.wireOp",EDGE,"E21.filletArc");var subQ1=sQuery(id+"F0.wireOp",EDGE,"E7");var subQ2=sQuery(id+"F0.wireOp",EDGE,"E6");var subQ3=sQuery(id+"F0.wireOp",EDGE,"E5");var subQ4=sQuery(id+"F0.wireOp",EDGE,"E4");var subQ5=sQuery(id+"F0.wireOp",EDGE,"E22.filletArc");var subQ6=sQuery(id+"F0.wireOp",EDGE,"E1.bottom");var subQ7=sQuery(id+"F0.wireOp",EDGE,"E1.right");var subQ8=sQuery(id+"F0.wireOp",EDGE,"E1.top");var subQ9=sQuery(id+"F0.wireOp",EDGE,"E1.left");var subQ10=sQuery(id+"F0.wireOp",EDGE,"E23.filletArc");var subQ11=sQuery(id+"F0.wireOp",EDGE,"E24.filletArc");Q0=makeQuery(id+"F2.boolean.opBoolean","SPLIT",FACE,{"disambiguationData":[TD([makeQuery(id+"F1.opExtrude","SWEPT_FACE",FACE,{"disambiguationData":[OSD([subQ6])]})])],"derivedFrom":makeQuery(id+"F1.opExtrude","CAP_FACE",FACE,{"disambiguationData":[OSD([subQ6,subQ8,subQ9,subQ7,subQ4,subQ3,subQ2,subQ1,subQ0,subQ5,subQ10,subQ11])],"isStart":true})});}
            var sketch = newSketch(context, id + "F16", { "sketchPlane" : qUnion([Q0])});
            skArc(sketch, "E79.0.1", {"start": v(-70, 90) * mm, "mid": v(-77.07, 87.07) * mm, "end": v(-80, 80) * mm});
            skLineSegment(sketch, "E79.0.2", {"start": v(-80, 80) * mm, "end": v(-80, -80) * mm});
            skArc(sketch, "E79.0.3", {"start": v(-80, -80) * mm, "mid": v(-77.07, -87.07) * mm, "end": v(-70, -90) * mm});
            skLineSegment(sketch, "E79.0.4", {"start": v(-70, -90) * mm, "end": v(70, -90) * mm});
            skArc(sketch, "E79.0.5", {"start": v(70, -90) * mm, "mid": v(77.07, -87.07) * mm, "end": v(80, -80) * mm});
            skLineSegment(sketch, "E79.0.6", {"start": v(80, -80) * mm, "end": v(80, 80) * mm});
            skArc(sketch, "E79.0.7", {"start": v(80, 80) * mm, "mid": v(77.07, 87.07) * mm, "end": v(70, 90) * mm});
            skCircle(sketch, "E80", {"center": v(0, 120) * mm, "radius": 6 * mm});
            skLineSegment(sketch, "E81", {"start": v(15, 108) * mm, "end": v(33, 90) * mm});
            skLineSegment(sketch, "E82", {"start": v(-15, 108) * mm, "end": v(-15, 120) * mm});
            skLineSegment(sketch, "E83", {"start": v(15, 108) * mm, "end": v(15, 120) * mm});
            skArc(sketch, "E84", {"start": v(15, 120) * mm, "mid": v(0, 135) * mm, "end": v(-15, 120) * mm});
            skLineSegment(sketch, "E85", {"start": v(0, 90) * mm, "end": v(0, 120) * mm, "construction": true});
            skLineSegment(sketch, "E86", {"start": v(-15, 108) * mm, "end": v(-33, 90) * mm});
            skLineSegment(sketch, "E87", {"start": v(-33, 90) * mm, "end": v(33, 90) * mm});
            skLineSegment(sketch, "E88", {"start": v(-80, 0) * mm, "end": v(80, 0) * mm, "construction": true});
            skLineSegment(sketch, "E89.MirrorCS", {"start": v(-15, -108) * mm, "end": v(-33, -90) * mm});
            skLineSegment(sketch, "E90.MirrorCS", {"start": v(15, -108) * mm, "end": v(33, -90) * mm});
            skLineSegment(sketch, "E91.MirrorCS", {"start": v(15, -108) * mm, "end": v(15, -120) * mm});
            skLineSegment(sketch, "E92.MirrorCS", {"start": v(-15, -108) * mm, "end": v(-15, -120) * mm});
            skArc(sketch, "E93.MirrorCS", {"start": v(15, -120) * mm, "mid": v(0, -135) * mm, "end": v(-15, -120) * mm});
            skCircle(sketch, "E94.MirrorC", {"center": v(0, -120) * mm, "radius": 6 * mm});
            skLineSegment(sketch, "E95.MirrorCS", {"start": v(0, -90) * mm, "end": v(0, -120) * mm, "construction": true});
            skCircle(sketch, "E96.0", {"center": v(-60, 67.5) * mm, "radius": 4 * mm});
            skCircle(sketch, "E97.0", {"center": v(60, 67.5) * mm, "radius": 4 * mm});
            skCircle(sketch, "E98.0", {"center": v(60, -67.5) * mm, "radius": 4 * mm});
            skCircle(sketch, "E99.0", {"center": v(-60, -67.5) * mm, "radius": 4 * mm});
            skLineSegment(sketch, "E100.0", {"start": v(-70, 90) * mm, "end": v(70, 90) * mm});
            skArc(sketch, "E101.0", {"start": v(56.15, 48.18) * mm, "mid": v(0, 67.5) * mm, "end": v(-56.15, 48.18) * mm});
            skArc(sketch, "E102.0", {"start": v(-56.15, 48.18) * mm, "mid": v(-58.99, 44.68) * mm, "end": v(-60, 40.3) * mm});
            skLineSegment(sketch, "E103.0", {"start": v(-60, 40.3) * mm, "end": v(-60, -40.3) * mm});
            skArc(sketch, "E104.0", {"start": v(-60, -40.3) * mm, "mid": v(-58.99, -44.68) * mm, "end": v(-56.15, -48.18) * mm});
            skArc(sketch, "E105.0", {"start": v(-56.15, -48.18) * mm, "mid": v(0, -67.5) * mm, "end": v(56.15, -48.18) * mm});
            skArc(sketch, "E106.0", {"start": v(56.15, -48.18) * mm, "mid": v(58.99, -44.68) * mm, "end": v(60, -40.3) * mm});
            skLineSegment(sketch, "E107.0", {"start": v(60, 40.3) * mm, "end": v(60, -40.3) * mm});
            skArc(sketch, "E108.0", {"start": v(60, 40.3) * mm, "mid": v(58.99, 44.68) * mm, "end": v(56.15, 48.18) * mm});
            skSolve(sketch);
        }
        {
            var Q0;
            Q0 = qSketchRegion(id + "F16", true);
            extrude(context, id + "F17", {"entities" : qUnion([Q0]), "depth" : 3 * mm, "offsetDistance" : 25 * mm});
        }
    });
